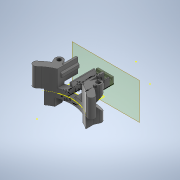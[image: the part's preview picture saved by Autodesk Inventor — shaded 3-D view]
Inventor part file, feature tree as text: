
AUTODESK INVENTOR PART (.ipt)
format: ipt  version: 2020 (Build 240168000, 168)  size: 668,160 bytes
history: native  units: mm
features: extrude x13, sketch x13, projected_geometry x10, other x3, sweep x1
ambient origin geometry x8: Origin, YZ Plane, XZ Plane, XY Plane, X Axis, Y Axis, Z Axis, Center Point
bodies: Body1 (feature_tree), Body2 (feature_tree), Body3 (feature_tree)
feature tree (40):
  other  "Твердое тело1"
  extrude  "Выдавливание1"  Depth=35.0mm TaperAngle=0.0deg
  sketch  "Эскиз2"
  extrude  "Выдавливание2"  Depth=4.0mm
  sweep  "Сдвиг1"
  extrude  "Выдавливание5"  Depth=8.0mm
  extrude  "Выдавливание6"  Depth=35.0mm TaperAngle=0.0deg
  extrude  "Выдавливание7"  Depth=8.5mm
  extrude  "Выдавливание8"  TaperAngle=45.0deg  [1 undecoded]
  other  "РабПлоскость1"
  extrude  "Выдавливание9"  Depth=8.5mm
  extrude  "Выдавливание10"  TaperAngle=45.0deg  [1 undecoded]
  extrude  "Выдавливание11"  TaperAngle=0.0deg  [1 undecoded]
  sketch  "Эскиз14"
  extrude  "Выдавливание12"  Depth=15.0mm TaperAngle=0.0deg
  extrude  "Выдавливание13"  Depth=5.0mm TaperAngle=0.0deg
  other  "РабПлоскость2"
  extrude  "Выдавливание14"  Depth=15.0mm TaperAngle=0.0deg
  extrude  "Выдавливание15"  Depth=26.0mm
  sketch  "Эскиз17"
  sketch  "Эскиз1"
  sketch  "Эскиз3"
  projected_geometry  "Спроецированная петля1"
  projected_geometry  "Спроецированная петля2"
  sketch  "3D эскиз1"
  sketch  "Эскиз4"
  sketch  "Эскиз6"
  projected_geometry  "Спроецированная петля4"
  sketch  "Эскиз7"
  projected_geometry  "Спроецированная петля5"
  sketch  "Эскиз9"
  projected_geometry  "Спроецированная петля7"
  sketch  "Эскиз11"
  projected_geometry  "Спроецированная петля8"
  sketch  "Эскиз12"
  projected_geometry  "Спроецированная петля9"
  projected_geometry  "Спроецированная петля10"
  sketch  "Эскиз16"
  projected_geometry  "Спроецированная петля15"
  projected_geometry  "Спроецированная петля16"
note: 3 required parameter values undecoded (feature->parameter linkage not recoverable at this tier; creation-order binding heuristic only, values carry confidence <= 0.55)
